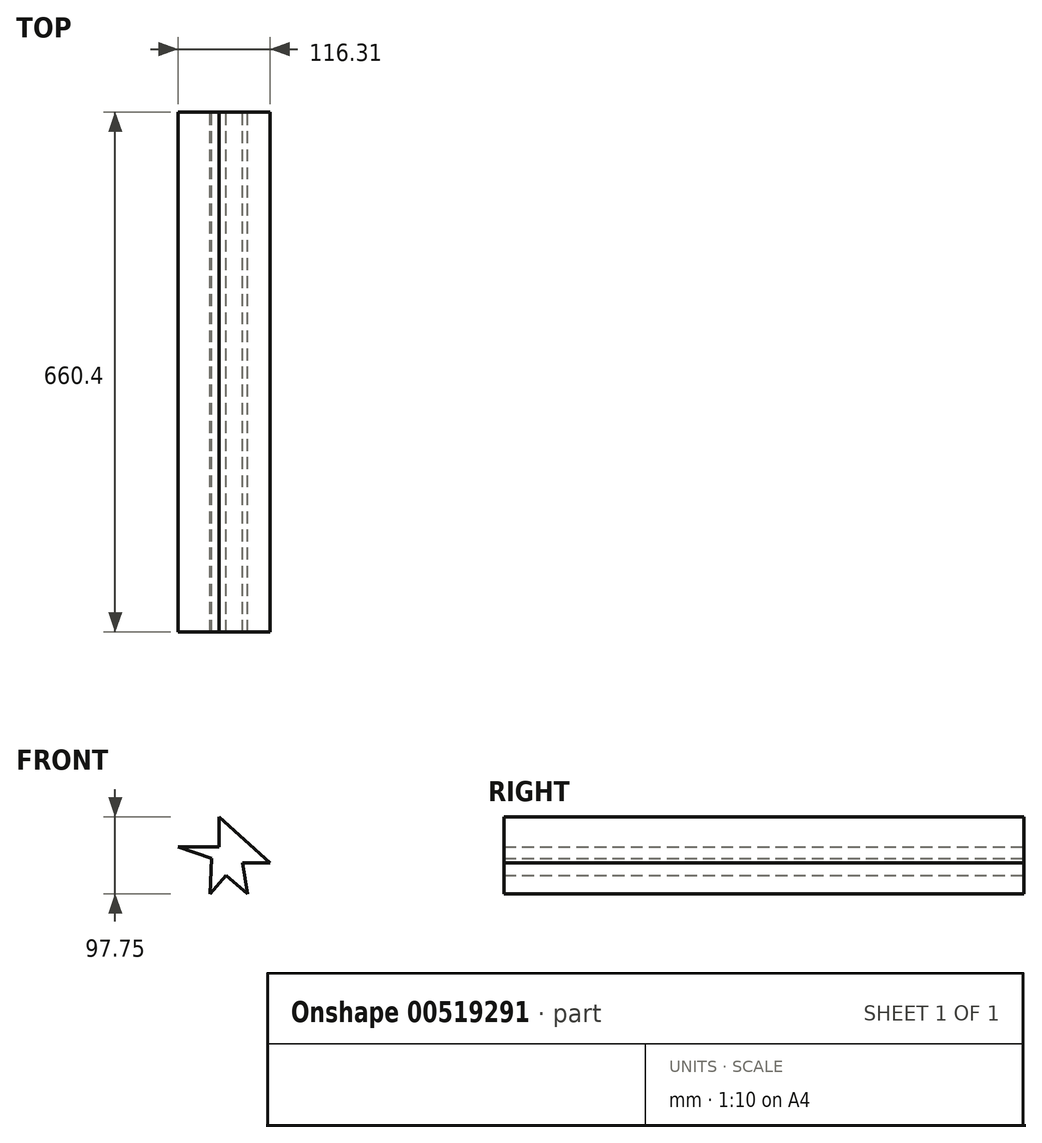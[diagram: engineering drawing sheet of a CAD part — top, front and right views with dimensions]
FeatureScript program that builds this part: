
annotation { "Feature Type Name" : "Feature", "Feature Type Description" : "" }
export const myFeature = defineFeature(function(context is Context, id is Id, definition is map)
    precondition{}
    {
        {
            var Q0;
            Q0=qCreatedBy(makeId("Front.planeOp"),FACE);
            var sketch = newSketch(context, id + "F0", { "sketchPlane" : qUnion([Q0])});
            skLineSegment(sketch, "E0", {"start": v(-7.63, -25.03) * mm, "end": v(-28.04, -48.6) * mm});
            skLineSegment(sketch, "E1", {"start": v(-28.04, -48.6) * mm, "end": v(-26.25, -3.36) * mm});
            skLineSegment(sketch, "E2", {"start": v(-7.63, -25.03) * mm, "end": v(19.6, -48.6) * mm});
            skLineSegment(sketch, "E3", {"start": v(19.6, -48.6) * mm, "end": v(13.13, -9.16) * mm});
            skLineSegment(sketch, "E4", {"start": v(13.13, -9.16) * mm, "end": v(47.93, -9.16) * mm});
            skLineSegment(sketch, "E5", {"start": v(47.93, -9.16) * mm, "end": v(-16.48, 49.15) * mm});
            skLineSegment(sketch, "E6", {"start": v(-16.48, 49.15) * mm, "end": v(-16.48, 10.99) * mm});
            skLineSegment(sketch, "E7", {"start": v(-16.48, 10.99) * mm, "end": v(-68.38, 10.99) * mm});
            skLineSegment(sketch, "E8", {"start": v(-68.38, 10.99) * mm, "end": v(-26.25, -3.36) * mm});
            skSolve(sketch);
        }
        {
            var Q0;
            Q0=makeQuery(id+"F0.imprint","IMPRINT",FACE,{"disambiguationData":[TD([[makeQuery(id+"F0.imprint","IMPRINT",EDGE,{"derivedFrom":sQuery(id+"F0.wireOp",EDGE,"E0")}),-1.0]])]});
            extrude(context, id + "F1", {"entities" : qUnion([Q0]), "depth" : 25.4 * mm, "offsetDistance" : 25.4 * mm});
        }
        {
            var Q0;
            Q0=makeQuery(id+"F1.opExtrude","CAP_FACE",FACE,{"disambiguationData":[OSD([sQuery(id+"F0.wireOp",EDGE,"E0"),sQuery(id+"F0.wireOp",EDGE,"E1"),sQuery(id+"F0.wireOp",EDGE,"E2"),sQuery(id+"F0.wireOp",EDGE,"E3"),sQuery(id+"F0.wireOp",EDGE,"E4"),sQuery(id+"F0.wireOp",EDGE,"E5"),sQuery(id+"F0.wireOp",EDGE,"E6"),sQuery(id+"F0.wireOp",EDGE,"E7"),sQuery(id+"F0.wireOp",EDGE,"E8")])],"isStart":false});
            extrude(context, id + "F2", {"entities" : qUnion([Q0]), "operationType" : NewBodyOperationType.ADD, "depth" : 609.6 * mm, "offsetDistance" : 25.4 * mm});
        }
        {
            var Q0;
            Q0=makeQuery(id+"F2.opExtrude","CAP_FACE",FACE,{"disambiguationData":[OSD([sQuery(id+"F0.wireOp",EDGE,"E0"),sQuery(id+"F0.wireOp",EDGE,"E1"),sQuery(id+"F0.wireOp",EDGE,"E2"),sQuery(id+"F0.wireOp",EDGE,"E3"),sQuery(id+"F0.wireOp",EDGE,"E4"),sQuery(id+"F0.wireOp",EDGE,"E5"),sQuery(id+"F0.wireOp",EDGE,"E6"),sQuery(id+"F0.wireOp",EDGE,"E7"),sQuery(id+"F0.wireOp",EDGE,"E8")])],"isStart":false});
            extrude(context, id + "F3", {"entities" : qUnion([Q0]), "operationType" : NewBodyOperationType.ADD, "depth" : 25.4 * mm, "offsetDistance" : 25.4 * mm});
        }
    });
